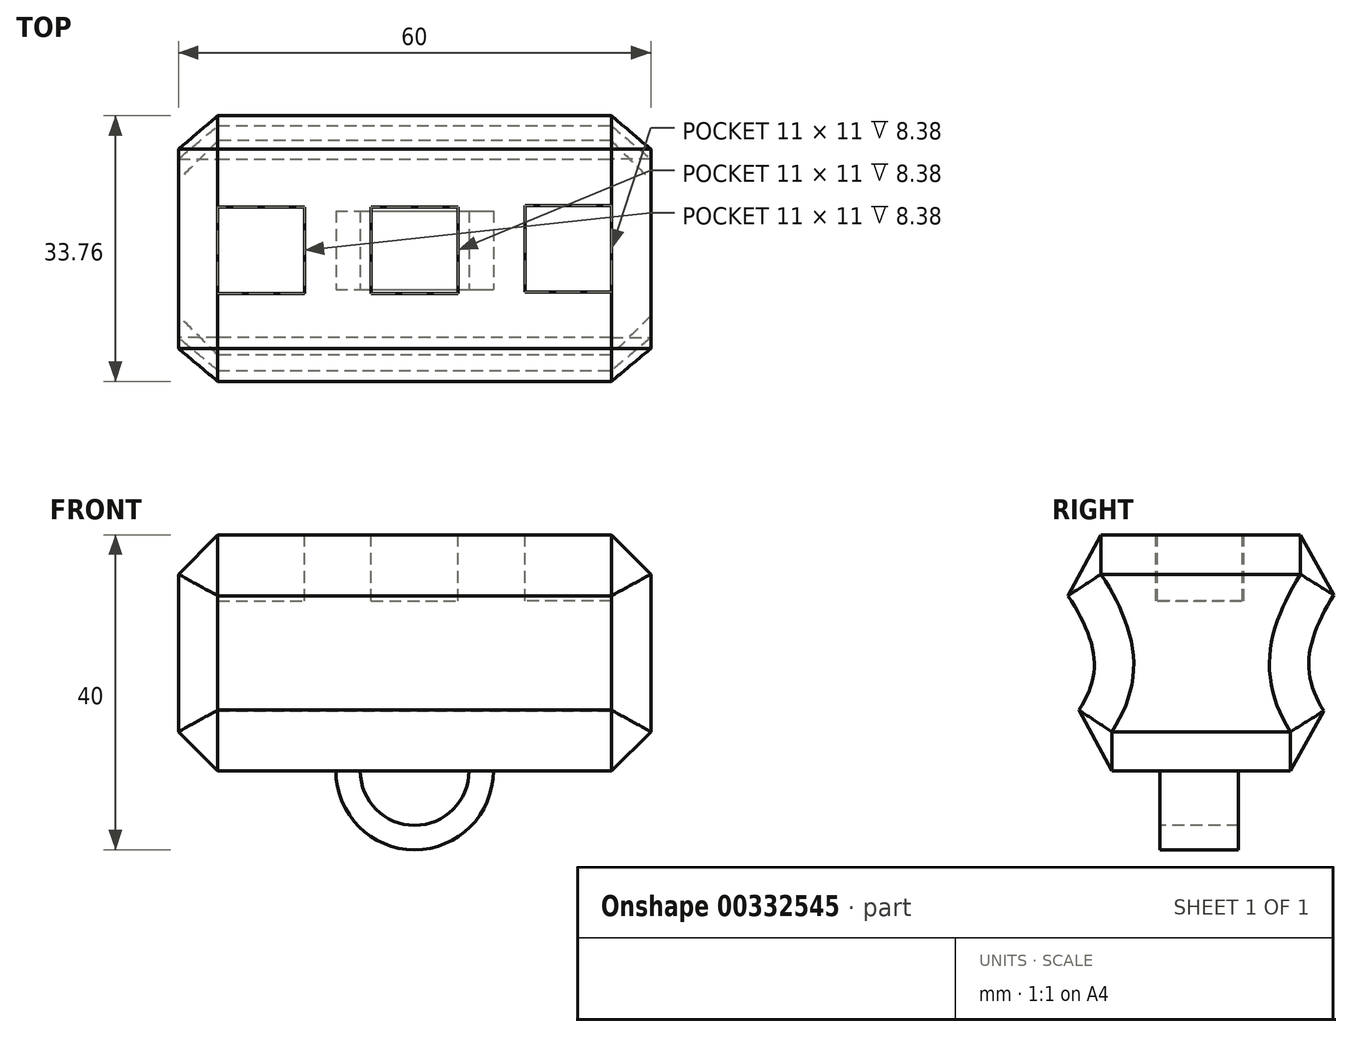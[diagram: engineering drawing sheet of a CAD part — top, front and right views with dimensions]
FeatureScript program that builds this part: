
annotation { "Feature Type Name" : "Feature", "Feature Type Description" : "" }
export const myFeature = defineFeature(function(context is Context, id is Id, definition is map)
    precondition{}
    {
        {
            var Q0;
            Q0=qCreatedBy(makeId("Top.planeOp"),FACE);
            var sketch = newSketch(context, id + "F0", { "sketchPlane" : qUnion([Q0])});
            skLineSegment(sketch, "E0.bottom", {"start": v(30, 22.5) * mm, "end": v(-30, 22.5) * mm});
            skLineSegment(sketch, "E0.top", {"start": v(30, -22.5) * mm, "end": v(-30, -22.5) * mm});
            skLineSegment(sketch, "E0.left", {"start": v(30, 22.5) * mm, "end": v(30, -22.5) * mm});
            skLineSegment(sketch, "E0.right", {"start": v(-30, 22.5) * mm, "end": v(-30, -22.5) * mm});
            skPoint(sketch, "E0.middle", {"position": v(0, 0) * mm});
            skLineSegment(sketch, "E1.bottom", {"start": v(-30, 22.5) * mm, "end": v(-42, 22.5) * mm});
            skLineSegment(sketch, "E1.top", {"start": v(-30, -22.5) * mm, "end": v(-42, -22.5) * mm});
            skLineSegment(sketch, "E1.right", {"start": v(-42, 22.5) * mm, "end": v(-42, -22.5) * mm});
            skLineSegment(sketch, "E2.bottom", {"start": v(30, 22.5) * mm, "end": v(42, 22.5) * mm});
            skLineSegment(sketch, "E2.top", {"start": v(30, -22.5) * mm, "end": v(42, -22.5) * mm});
            skLineSegment(sketch, "E2.right", {"start": v(42, 22.5) * mm, "end": v(42, -22.5) * mm});
            skSolve(sketch);
        }
        {
            var Q0;
            Q0=makeQuery(id+"F0.imprint","IMPRINT",FACE,{"disambiguationData":[TD([[makeQuery(id+"F0.imprint","IMPRINT",EDGE,{"derivedFrom":sQuery(id+"F0.wireOp",EDGE,"E0.bottom")}),1.0]])]});
            extrude(context, id + "F1", {"entities" : qUnion([Q0]), "depth" : 30 * mm});
        }
        {
            var Q0;
            Q0=makeQuery(id+"F1.opExtrude","SWEPT_FACE",FACE,{"disambiguationData":[OSD([sQuery(id+"F0.wireOp",EDGE,"E0.left")])]});
            var sketch = newSketch(context, id + "F2", { "sketchPlane" : qUnion([Q0])});
            skFitSpline(sketch, "E3", {"points": [v(22.5, 0) * mm, v(13.93, 13.04) * mm, v(22.5, 30) * mm], "startDerivative": vector(-26.19, 26.27) * mm, "endDerivative": vector(25.34, 33.61) * mm});
            skFitSpline(sketch, "E4", {"points": [v(-22.5, 0) * mm, v(-13.32, 13.01) * mm, v(-22.5, 30) * mm], "startDerivative": vector(28.03, 26.14) * mm, "endDerivative": vector(-27.15, 33.74) * mm});
            skSolve(sketch);
        }
        {
            var Q0;
            Q0=makeQuery(id+"F2.imprint","IMPRINT",FACE,{"disambiguationData":[TD([[makeQuery(id+"F2.imprint","IMPRINT",EDGE,{"derivedFrom":sQuery(id+"F2.wireOp",EDGE,"E4")}),1.0]])]});
            var Q1;
            Q1=makeQuery(id+"F2.imprint","IMPRINT",FACE,{"disambiguationData":[TD([[makeQuery(id+"F2.imprint","IMPRINT",EDGE,{"derivedFrom":sQuery(id+"F2.wireOp",EDGE,"E3")}),-1.0]])]});
            extrude(context, id + "F3", {"entities" : qUnion([Q0, Q1]), "operationType" : NewBodyOperationType.REMOVE, "endBound" : BoundingType.THROUGH_ALL, "oppositeDirection" : true, "depth" : 25 * mm});
        }
        {
            var Q0;
            Q0=makeQuery(id+"F1.opExtrude","SWEPT_FACE",FACE,{"disambiguationData":[OSD([sQuery(id+"F0.wireOp",EDGE,"E0.right")])]});
            var Q1;
            Q1=makeQuery(id+"F1.opExtrude","SWEPT_FACE",FACE,{"disambiguationData":[OSD([sQuery(id+"F0.wireOp",EDGE,"E0.left")])]});
            var Q2;
            Q2=makeQuery(id+"F1.opExtrude","CAP_FACE",FACE,{"disambiguationData":[OSD([sQuery(id+"F0.wireOp",EDGE,"E0.bottom"),sQuery(id+"F0.wireOp",EDGE,"E0.top"),sQuery(id+"F0.wireOp",EDGE,"E0.right"),sQuery(id+"F0.wireOp",EDGE,"E0.left")])],"isStart":false});
            var Q3;
            Q3=makeQuery(id+"F1.opExtrude","CAP_FACE",FACE,{"disambiguationData":[OSD([sQuery(id+"F0.wireOp",EDGE,"E0.bottom"),sQuery(id+"F0.wireOp",EDGE,"E0.top"),sQuery(id+"F0.wireOp",EDGE,"E0.right"),sQuery(id+"F0.wireOp",EDGE,"E0.left")])],"isStart":true});
            chamfer(context, id + "F4", {"entities" : qUnion([Q0, Q1, Q2, Q3]), "width" : 5 * mm, "tangentPropagation" : true});
        }
        {
            var Q0;
            Q0=makeQuery(id+"F1.opExtrude","CAP_FACE",FACE,{"disambiguationData":[OSD([sQuery(id+"F0.wireOp",EDGE,"E0.bottom"),sQuery(id+"F0.wireOp",EDGE,"E0.top"),sQuery(id+"F0.wireOp",EDGE,"E0.right"),sQuery(id+"F0.wireOp",EDGE,"E0.left")])],"isStart":true});
            var sketch = newSketch(context, id + "F5", { "sketchPlane" : qUnion([Q0])});
            skLineSegment(sketch, "E5.bottom", {"start": v(10, 5) * mm, "end": v(-10, 5) * mm});
            skLineSegment(sketch, "E5.top", {"start": v(10, -5) * mm, "end": v(-10, -5) * mm});
            skLineSegment(sketch, "E5.left", {"start": v(10, 5) * mm, "end": v(10, -5) * mm});
            skLineSegment(sketch, "E5.right", {"start": v(-10, 5) * mm, "end": v(-10, -5) * mm});
            skPoint(sketch, "E5.middle", {"position": v(0, 0) * mm});
            skLineSegment(sketch, "E6", {"start": v(0, 5) * mm, "end": v(0, -5) * mm});
            skSolve(sketch);
        }
        {
            var Q0;
            {var subQ0=sQuery(id+"F5.wireOp",EDGE,"E5.right");Q0=makeQuery(id+"F5.imprint","IMPRINT",FACE,{"disambiguationData":[TD([[makeQuery(id+"F5.imprint","IMPRINT",EDGE,{"derivedFrom":subQ0}),1.0]])]});}
            var Q1;
            Q1=sQuery(id+"F5.wireOp",EDGE,"E6");
            revolve(context, id + "F6", {"operationType" : NewBodyOperationType.ADD, "entities" : qUnion([Q0]), "axis" : qUnion([Q1]), "revolveType" : RevolveType.FULL});
        }
        {
            var Q0;
            Q0=makeQuery(id+"F6.opRevolve","SWEPT_FACE",FACE,{"disambiguationData":[OSD([sQuery(id+"F5.wireOp",EDGE,"E5.bottom")])]});
            var sketch = newSketch(context, id + "F7", { "sketchPlane" : qUnion([Q0])});
            skCircle(sketch, "E7", {"center": v(0, 0) * mm, "radius": 6.9 * mm});
            skSolve(sketch);
        }
        {
            var Q0;
            {var subQ0=sQuery(id+"F7.wireOp",EDGE,"E7");var subQ1=makeQuery(id+"F6.boolean.opBoolean","INTERSECT",EDGE,{"derivedFrom":[makeQuery(id+"F1.opExtrude","CAP_FACE",FACE,{"disambiguationData":[OSD([sQuery(id+"F0.wireOp",EDGE,"E0.bottom"),sQuery(id+"F0.wireOp",EDGE,"E0.top"),sQuery(id+"F0.wireOp",EDGE,"E0.right"),sQuery(id+"F0.wireOp",EDGE,"E0.left")])],"isStart":true}),makeQuery(id+"F6.opRevolve","SWEPT_FACE",FACE,{"disambiguationData":[OSD([sQuery(id+"F5.wireOp",EDGE,"E5.bottom")])]})]});var subQ2=makeQuery(id+"F7.imprint","INTERSECT",VERTEX,{"disambiguationData":[OD(0.0)],"derivedFrom":[subQ1,subQ0]});Q0=makeQuery(id+"F7.imprint","IMPRINT",FACE,{"disambiguationData":[TD([[makeQuery(id+"F7.imprint","IMPRINT",EDGE,{"disambiguationData":[TD([[subQ2,-1.0]])],"derivedFrom":subQ0}),1.0]])]});}
            extrude(context, id + "F8", {"entities" : qUnion([Q0]), "operationType" : NewBodyOperationType.REMOVE, "endBound" : BoundingType.THROUGH_ALL, "oppositeDirection" : true, "depth" : 25 * mm});
        }
        {
            var Q0;
            Q0=makeQuery(id+"F1.opExtrude","CAP_FACE",FACE,{"disambiguationData":[OSD([sQuery(id+"F0.wireOp",EDGE,"E0.bottom"),sQuery(id+"F0.wireOp",EDGE,"E0.top"),sQuery(id+"F0.wireOp",EDGE,"E0.right"),sQuery(id+"F0.wireOp",EDGE,"E0.left")])],"isStart":false});
            var sketch = newSketch(context, id + "F9", { "sketchPlane" : qUnion([Q0])});
            skLineSegment(sketch, "E8.top", {"start": v(25, -5.32) * mm, "end": v(14, -5.32) * mm});
            skLineSegment(sketch, "E8.left", {"start": v(25, 0.18) * mm, "end": v(25, -5.32) * mm});
            skLineSegment(sketch, "E8.right", {"start": v(14, 0.18) * mm, "end": v(14, -5.32) * mm});
            skLineSegment(sketch, "E9.top", {"start": v(25, 5.68) * mm, "end": v(14, 5.68) * mm});
            skLineSegment(sketch, "E9.left", {"start": v(25, 0.18) * mm, "end": v(25, 5.68) * mm});
            skLineSegment(sketch, "E9.right", {"start": v(14, 0.18) * mm, "end": v(14, 5.68) * mm});
            skLineSegment(sketch, "E10", {"start": v(-25, 0) * mm, "end": v(-25, 5.5) * mm});
            skLineSegment(sketch, "E11", {"start": v(-25, 0) * mm, "end": v(-25, -5.5) * mm});
            skLineSegment(sketch, "E12", {"start": v(-25, 5.5) * mm, "end": v(-14, 5.5) * mm});
            skLineSegment(sketch, "E13", {"start": v(-14, 5.5) * mm, "end": v(-14, -5.5) * mm});
            skLineSegment(sketch, "E14", {"start": v(-25, -5.5) * mm, "end": v(-14, -5.5) * mm});
            skLineSegment(sketch, "E15.bottom", {"start": v(-5.5, 5.5) * mm, "end": v(5.5, 5.5) * mm});
            skLineSegment(sketch, "E15.top", {"start": v(-5.5, -5.5) * mm, "end": v(5.5, -5.5) * mm});
            skLineSegment(sketch, "E15.left", {"start": v(-5.5, 5.5) * mm, "end": v(-5.5, -5.5) * mm});
            skLineSegment(sketch, "E15.right", {"start": v(5.5, 5.5) * mm, "end": v(5.5, -5.5) * mm});
            skPoint(sketch, "E15.middle", {"position": v(0, 0) * mm});
            skSolve(sketch);
        }
        {
            var Q0;
            Q0=makeQuery(id+"F9.imprint","IMPRINT",FACE,{"disambiguationData":[TD([[makeQuery(id+"F9.imprint","IMPRINT",EDGE,{"derivedFrom":sQuery(id+"F9.wireOp",EDGE,"E10")}),1.0]])]});
            var Q1;
            Q1=makeQuery(id+"F9.imprint","IMPRINT",FACE,{"disambiguationData":[TD([[makeQuery(id+"F9.imprint","IMPRINT",EDGE,{"derivedFrom":sQuery(id+"F9.wireOp",EDGE,"E15.bottom")}),-1.0]])]});
            var Q2;
            Q2=makeQuery(id+"F9.imprint","IMPRINT",FACE,{"disambiguationData":[TD([[makeQuery(id+"F9.imprint","IMPRINT",EDGE,{"derivedFrom":sQuery(id+"F9.wireOp",EDGE,"E8.top")}),-1.0]])]});
            extrude(context, id + "F10", {"entities" : qUnion([Q0, Q1, Q2]), "operationType" : NewBodyOperationType.REMOVE, "oppositeDirection" : true, "depth" : 8.38 * mm});
        }
    });
